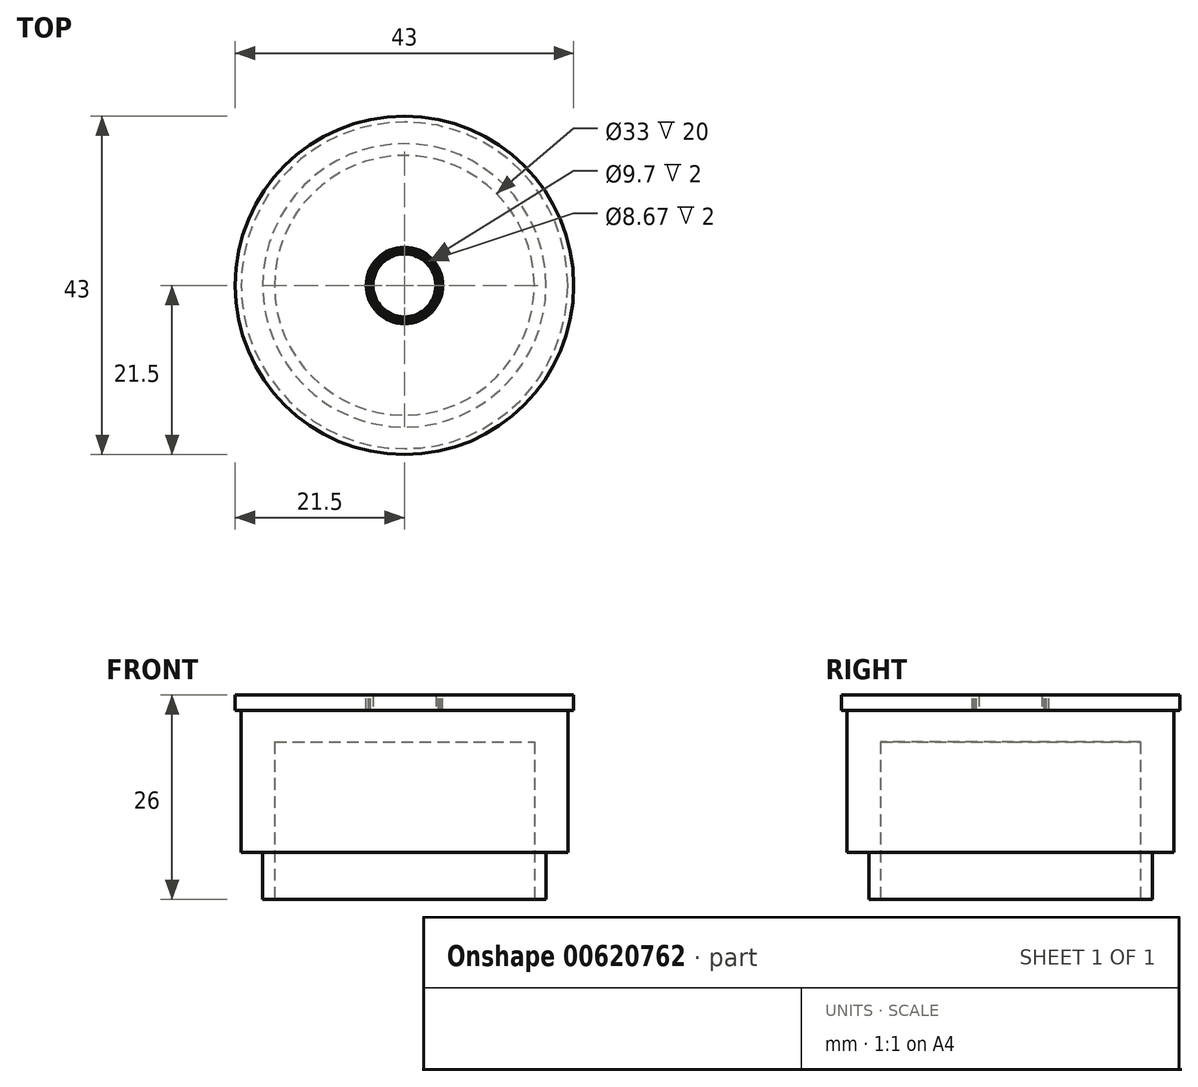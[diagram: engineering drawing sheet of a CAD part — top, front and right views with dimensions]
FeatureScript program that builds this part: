
annotation { "Feature Type Name" : "Feature", "Feature Type Description" : "" }
export const myFeature = defineFeature(function(context is Context, id is Id, definition is map)
    precondition{}
    {
        {
            var Q0;
            Q0=qCreatedBy(makeId("Top.planeOp"),FACE);
            var sketch = newSketch(context, id + "F0", { "sketchPlane" : qUnion([Q0])});
            skCircle(sketch, "E0", {"center": v(0, 0) * mm, "radius": 20.75 * mm});
            skSolve(sketch);
        }
        {
            var Q0;
            Q0=makeQuery(id+"F0.imprint","IMPRINT",FACE,{"disambiguationData":[TD([[makeQuery(id+"F0.imprint","IMPRINT",EDGE,{"derivedFrom":sQuery(id+"F0.wireOp",EDGE,"E0")}),1.0]])]});
            extrude(context, id + "F1", {"entities" : qUnion([Q0]), "depth" : 20 * mm, "offsetDistance" : 25 * mm});
        }
        {
            var Q0;
            Q0=makeQuery(id+"F1.opExtrude","CAP_FACE",FACE,{"disambiguationData":[OSD([sQuery(id+"F0.wireOp",EDGE,"E0")])],"isStart":true});
            var sketch = newSketch(context, id + "F2", { "sketchPlane" : qUnion([Q0])});
            skCircle(sketch, "E1", {"center": v(0, 0) * mm, "radius": 18 * mm});
            skSolve(sketch);
        }
        {
            var Q0;
            Q0=makeQuery(id+"F2.imprint","IMPRINT",FACE,{"disambiguationData":[TD([[makeQuery(id+"F2.imprint","IMPRINT",EDGE,{"derivedFrom":sQuery(id+"F2.wireOp",EDGE,"E1")}),1.0]])]});
            extrude(context, id + "F3", {"entities" : qUnion([Q0]), "operationType" : NewBodyOperationType.ADD, "depth" : 6 * mm, "offsetDistance" : 25 * mm});
        }
        {
            var Q0;
            Q0=makeQuery(id+"F1.opExtrude","CAP_FACE",FACE,{"disambiguationData":[OSD([sQuery(id+"F0.wireOp",EDGE,"E0")])],"isStart":false});
            var sketch = newSketch(context, id + "F4", { "sketchPlane" : qUnion([Q0])});
            skCircle(sketch, "E2", {"center": v(0, 0) * mm, "radius": 21.5 * mm});
            skSolve(sketch);
        }
        {
            var Q0;
            Q0 = qSketchRegion(id + "F4", true);
            extrude(context, id + "F5", {"entities" : qUnion([Q0]), "operationType" : NewBodyOperationType.ADD, "oppositeDirection" : true, "depth" : 2 * mm, "offsetDistance" : 25 * mm});
        }
        {
            var Q0;
            Q0=makeQuery(id+"F5.boolean.opBoolean","MERGE",FACE,{"derivedFrom":[makeQuery(id+"F1.opExtrude","CAP_FACE",FACE,{"disambiguationData":[OSD([sQuery(id+"F0.wireOp",EDGE,"E0")])],"isStart":false}),makeQuery(id+"F5.opExtrude","CAP_FACE",FACE,{"disambiguationData":[OSD([sQuery(id+"F4.wireOp",EDGE,"E2")])],"isStart":true})]});
            var sketch = newSketch(context, id + "F6", { "sketchPlane" : qUnion([Q0])});
            skCircle(sketch, "E3", {"center": v(0, 0) * mm, "radius": 4.33 * mm});
            skSolve(sketch);
        }
        {
            var Q0;
            Q0 = qSketchRegion(id + "F6", true);
            extrude(context, id + "F7", {"entities" : qUnion([Q0]), "operationType" : NewBodyOperationType.REMOVE, "oppositeDirection" : true, "depth" : 2 * mm, "offsetDistance" : 25 * mm});
        }
        {
            var Q0;
            Q0=makeQuery(id+"F3.opExtrude","CAP_FACE",FACE,{"disambiguationData":[OSD([sQuery(id+"F2.wireOp",EDGE,"E1")])],"isStart":false});
            var sketch = newSketch(context, id + "F8", { "sketchPlane" : qUnion([Q0])});
            skCircle(sketch, "E4", {"center": v(0, 0) * mm, "radius": 16.5 * mm});
            skSolve(sketch);
        }
        {
            var Q0;
            Q0=makeQuery(id+"F8.imprint","IMPRINT",FACE,{"disambiguationData":[TD([[makeQuery(id+"F8.imprint","IMPRINT",EDGE,{"derivedFrom":sQuery(id+"F8.wireOp",EDGE,"E4")}),1.0]])]});
            extrude(context, id + "F9", {"entities" : qUnion([Q0]), "operationType" : NewBodyOperationType.REMOVE, "oppositeDirection" : true, "depth" : 20 * mm, "offsetDistance" : 25 * mm});
        }
        {
            var Q0;
            Q0=makeQuery(id+"F5.boolean.opBoolean","MERGE",FACE,{"derivedFrom":[makeQuery(id+"F1.opExtrude","CAP_FACE",FACE,{"disambiguationData":[OSD([sQuery(id+"F0.wireOp",EDGE,"E0")])],"isStart":false}),makeQuery(id+"F5.opExtrude","CAP_FACE",FACE,{"disambiguationData":[OSD([sQuery(id+"F4.wireOp",EDGE,"E2")])],"isStart":true})]});
            var sketch = newSketch(context, id + "F10", { "sketchPlane" : qUnion([Q0])});
            skCircle(sketch, "E5", {"center": v(0, 0) * mm, "radius": 4.58 * mm});
            skCircle(sketch, "E6", {"center": v(0, 0) * mm, "radius": 4.85 * mm});
            skSolve(sketch);
        }
        {
            var Q0;
            Q0=makeQuery(id+"F10.imprint","IMPRINT",FACE,{"disambiguationData":[TD([[makeQuery(id+"F10.imprint","IMPRINT",EDGE,{"derivedFrom":sQuery(id+"F10.wireOp",EDGE,"E5")}),-1.0]])]});
            extrude(context, id + "F11", {"entities" : qUnion([Q0]), "operationType" : NewBodyOperationType.REMOVE, "oppositeDirection" : true, "depth" : 2 * mm, "offsetDistance" : 25 * mm});
        }
        {
            var Q0;
            Q0=makeQuery(id+"F7.boolean.opBoolean","COPY",FACE,{"derivedFrom":makeQuery(id+"F7.opExtrude","CAP_FACE",FACE,{"disambiguationData":[OSD([sQuery(id+"F6.wireOp",EDGE,"E3")])],"isStart":false})});
            var sketch = newSketch(context, id + "F12", { "sketchPlane" : qUnion([Q0])});
            skCircle(sketch, "E7", {"center": v(0, 0) * mm, "radius": 4 * mm});
            skSolve(sketch);
        }
        {
            var Q0;
            Q0 = qSketchRegion(id + "F12", true);
            extrude(context, id + "F13", {"entities" : qUnion([Q0]), "operationType" : NewBodyOperationType.ADD, "depth" : 2 * mm, "offsetDistance" : 25 * mm});
        }
    });
